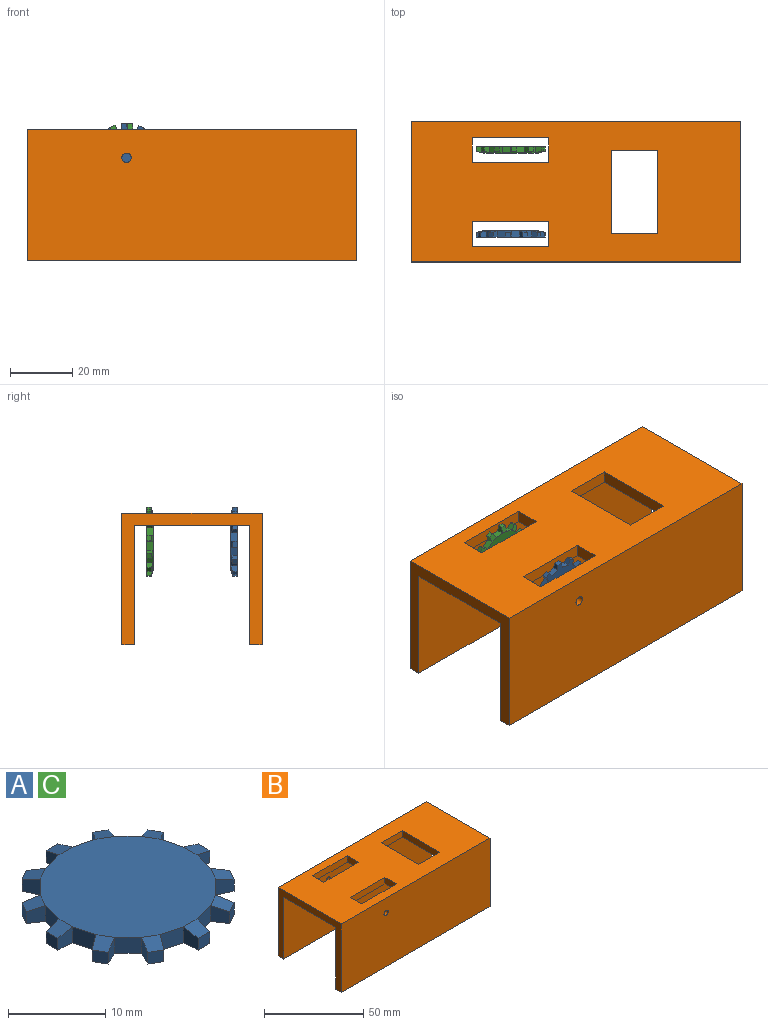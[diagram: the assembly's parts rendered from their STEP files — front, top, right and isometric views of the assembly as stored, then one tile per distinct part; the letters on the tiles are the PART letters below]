
ASSEMBLY  parts=3 mates=2
PART A: 62 faces, bbox 22.1x22.1x2 mm
  f0: plane 2.67x2mm, normal (0.26,0.97,0), area 5.5mm2, adj f1,f2,f5,f8
  f1: plane 18.09x18.09mm, normal (0,0,1), area 256.9mm2, adj f0,f4,f7,f9,f12,f14,f17,f19
  f2: plane 22.09x22.09mm, normal (0,0,-1), area 301.1mm2, adj f0,f3,f5,f6,f7,f8,f10,f11
  f3: plane 2x2mm, normal (-1,0.07,0), area 3.5mm2, adj f2,f4,f6,f57
  f4: plane 2x1.98mm, normal (0,0.26,0.97), area 3.8mm2, adj f1,f3,f5,f6
  f5: plane 2x2mm, normal (1,0.07,0), area 3.5mm2, adj f0,f2,f4,f6
  f6: plane 1.7x1.46mm, normal (0,1,0), area 2.5mm2, adj f2,f3,f4,f5
  f7: plane 2x1.96mm, normal (0.71,0.71,0), area 5.5mm2, adj f1,f2,f10,f13
  f8: plane 2x1.66mm, normal (-0.83,0.56,0), area 3.5mm2, adj f0,f2,f9,f11
  f9: plane 2.65x2.59mm, normal (0.13,0.22,0.97), area 3.8mm2, adj f1,f8,f10,f11
  f10: plane 2x1.8mm, normal (0.9,-0.44,0), area 3.5mm2, adj f2,f7,f9,f11
  f11: plane 1.47x1.46mm, normal (0.5,0.87,0), area 2.5mm2, adj f2,f8,f9,f10
  f12: plane 2.67x2mm, normal (0.97,0.26,0), area 5.5mm2, adj f1,f2,f15,f18
  f13: plane 2x1.8mm, normal (-0.44,0.9,0), area 3.5mm2, adj f2,f7,f14,f16
  f14: plane 2.65x2.59mm, normal (0.22,0.13,0.97), area 3.8mm2, adj f1,f13,f15,f16
  f15: plane 2x1.66mm, normal (0.56,-0.83,0), area 3.5mm2, adj f2,f12,f14,f16
  f16: plane 1.47x1.46mm, normal (0.87,0.5,0), area 2.5mm2, adj f2,f13,f14,f15
  f17: plane 2.67x2mm, normal (0.97,-0.26,0), area 5.5mm2, adj f1,f2,f20,f23
  f18: plane 2x2mm, normal (0.07,1,0), area 3.5mm2, adj f2,f12,f19,f21
  f19: plane 2x1.98mm, normal (0.26,0,0.97), area 3.8mm2, adj f1,f18,f20,f21
  f20: plane 2x2mm, normal (0.07,-1,0), area 3.5mm2, adj f2,f17,f19,f21
  f21: plane 1.7x1.46mm, normal (1,0,0), area 2.5mm2, adj f2,f18,f19,f20
  f22: plane 2x1.96mm, normal (0.71,-0.71,0), area 5.5mm2, adj f1,f2,f25,f28
  f23: plane 2x1.66mm, normal (0.56,0.83,0), area 3.5mm2, adj f2,f17,f24,f26
  f24: plane 2.65x2.59mm, normal (0.22,-0.13,0.97), area 3.8mm2, adj f1,f23,f25,f26
  f25: plane 2x1.8mm, normal (-0.44,-0.9,0), area 3.5mm2, adj f2,f22,f24,f26
  f26: plane 1.47x1.46mm, normal (0.87,-0.5,0), area 2.5mm2, adj f2,f23,f24,f25
  f27: plane 2.67x2mm, normal (0.26,-0.97,0), area 5.5mm2, adj f1,f2,f30,f33
  f28: plane 2x1.8mm, normal (0.9,0.44,0), area 3.5mm2, adj f2,f22,f29,f31
  f29: plane 2.65x2.59mm, normal (0.13,-0.22,0.97), area 3.8mm2, adj f1,f28,f30,f31
  f30: plane 2x1.66mm, normal (-0.83,-0.56,0), area 3.5mm2, adj f2,f27,f29,f31
  f31: plane 1.47x1.46mm, normal (0.5,-0.87,0), area 2.5mm2, adj f2,f28,f29,f30
  f32: plane 2.67x2mm, normal (-0.26,-0.97,0), area 5.5mm2, adj f1,f2,f35,f38
  f33: plane 2x2mm, normal (1,-0.07,0), area 3.5mm2, adj f2,f27,f34,f36
  f34: plane 2x1.98mm, normal (0,-0.26,0.97), area 3.8mm2, adj f1,f33,f35,f36
  f35: plane 2x2mm, normal (-1,-0.07,0), area 3.5mm2, adj f2,f32,f34,f36
  f36: plane 1.7x1.46mm, normal (0,-1,0), area 2.5mm2, adj f2,f33,f34,f35
  f37: plane 2x1.96mm, normal (-0.71,-0.71,0), area 5.5mm2, adj f1,f2,f40,f43
  f38: plane 2x1.66mm, normal (0.83,-0.56,0), area 3.5mm2, adj f2,f32,f39,f41
  f39: plane 2.65x2.59mm, normal (-0.13,-0.22,0.97), area 3.8mm2, adj f1,f38,f40,f41
  f40: plane 2x1.8mm, normal (-0.9,0.44,0), area 3.5mm2, adj f2,f37,f39,f41
  f41: plane 1.47x1.46mm, normal (-0.5,-0.87,0), area 2.5mm2, adj f2,f38,f39,f40
  f42: plane 2.67x2mm, normal (-0.97,-0.26,0), area 5.5mm2, adj f1,f2,f45,f48
  f43: plane 2x1.8mm, normal (0.44,-0.9,0), area 3.5mm2, adj f2,f37,f44,f46
  f44: plane 2.65x2.59mm, normal (-0.22,-0.13,0.97), area 3.8mm2, adj f1,f43,f45,f46
  f45: plane 2x1.66mm, normal (-0.56,0.83,0), area 3.5mm2, adj f2,f42,f44,f46
  f46: plane 1.47x1.46mm, normal (-0.87,-0.5,0), area 2.5mm2, adj f2,f43,f44,f45
  f47: plane 2.67x2mm, normal (-0.97,0.26,0), area 5.5mm2, adj f1,f2,f50,f53
  f48: plane 2x2mm, normal (-0.07,-1,0), area 3.5mm2, adj f2,f42,f49,f51
  f49: plane 2x1.98mm, normal (-0.26,0,0.97), area 3.8mm2, adj f1,f48,f50,f51
  f50: plane 2x2mm, normal (-0.07,1,0), area 3.5mm2, adj f2,f47,f49,f51
  f51: plane 1.7x1.46mm, normal (-1,0,0), area 2.5mm2, adj f2,f48,f49,f50
  f52: plane 2x1.96mm, normal (-0.71,0.71,0), area 5.5mm2, adj f1,f2,f55,f58
  f53: plane 2x1.66mm, normal (-0.56,-0.83,0), area 3.5mm2, adj f2,f47,f54,f56
  f54: plane 2.65x2.59mm, normal (-0.22,0.13,0.97), area 3.8mm2, adj f1,f53,f55,f56
  f55: plane 2x1.8mm, normal (0.44,0.9,0), area 3.5mm2, adj f2,f52,f54,f56
  f56: plane 1.47x1.46mm, normal (-0.87,0.5,0), area 2.5mm2, adj f2,f53,f54,f55
  f57: plane 2.67x2mm, normal (-0.26,0.97,0), area 5.5mm2, adj f1,f2,f3,f60
  f58: plane 2x1.8mm, normal (-0.9,-0.44,0), area 3.5mm2, adj f2,f52,f59,f61
  f59: plane 2.65x2.59mm, normal (-0.13,0.22,0.97), area 3.8mm2, adj f1,f58,f60,f61
  f60: plane 2x1.66mm, normal (0.83,0.56,0), area 3.5mm2, adj f2,f57,f59,f61
  f61: plane 1.47x1.46mm, normal (-0.5,0.87,0), area 2.5mm2, adj f2,f58,f59,f60
PART B: 24 faces, bbox 105.7x45x42.2 mm
  f0: plane 105.74x37mm, normal (0,0,-1), area 3116.2mm2, adj f1,f2,f3,f4,f5,f6,f7,f9
  f1: plane 8x4mm, normal (1,0,0), area 32mm2, adj f0,f2,f10,f11
  f2: plane 24.63x4mm, normal (0,-1,0), area 98.5mm2, adj f0,f1,f3,f11
  f3: plane 8x4mm, normal (-1,0,0), area 32mm2, adj f0,f2,f10,f11
  f4: plane 26.79x4mm, normal (-1,0,0), area 107.2mm2, adj f0,f5,f11,f18
  f5: plane 15x4mm, normal (0,1,0), area 60mm2, adj f0,f4,f6,f11
  f6: plane 26.79x4mm, normal (1,0,0), area 107.2mm2, adj f0,f5,f11,f18
  f7: plane 45x42.16mm, normal (-1,0,0), area 485.3mm2, adj f0,f8,f11,f13,f14,f19,f22,f23
  f8: plane 105.74x42.16mm, normal (0,-1,0), area 4450.7mm2, adj f7,f9,f11,f12,f13
  f9: plane 45x42.16mm, normal (1,0,0), area 485.3mm2, adj f0,f8,f11,f13,f14,f19,f22,f23
  f10: plane 24.63x4mm, normal (0,1,0), area 98.5mm2, adj f0,f1,f3,f11
  f11: plane 105.74x45mm, normal (0,0,1), area 3962.1mm2, adj f1,f2,f3,f4,f5,f6,f7,f8
  f12: cylinder r=1.5mm len=4mm, axis (0,-1,0), area 37.7mm2, adj f8,f14
  f13: plane 105.74x4mm, normal (0,0,-1), area 422.9mm2, adj f7,f8,f9,f14
  f14: plane 105.74x38.16mm, normal (0,1,0), area 4027.8mm2, adj f0,f7,f9,f12,f13
  f15: plane 8x4mm, normal (1,0,0), area 32mm2, adj f0,f11,f16,f20
  f16: plane 24.63x4mm, normal (0,1,0), area 98.5mm2, adj f0,f11,f15,f17
  f17: plane 8x4mm, normal (-1,0,0), area 32mm2, adj f0,f11,f16,f20
  f18: plane 15x4mm, normal (0,-1,0), area 60mm2, adj f0,f4,f6,f11
  f19: plane 105.74x42.16mm, normal (0,1,0), area 4450.7mm2, adj f7,f9,f11,f21,f22
  f20: plane 24.63x4mm, normal (0,-1,0), area 98.5mm2, adj f0,f11,f15,f17
  f21: cylinder r=1.5mm len=4mm, axis (0,1,0), area 37.7mm2, adj f19,f23
  f22: plane 105.74x4mm, normal (0,0,-1), area 422.9mm2, adj f7,f9,f19,f23
  f23: plane 105.74x38.16mm, normal (0,-1,0), area 4027.8mm2, adj f0,f7,f9,f21,f22
PART C: same geometry as A
PLACE A rot(axis=(-0.22,0.69,0.69),155.7deg) t=(-96.59,8,67.61)mm
PLACE B t=(-74.86,37.34,38.16)mm
PLACE C rot(axis=(0.73,0.48,-0.48),107.4deg) t=(-36.41,37,50.58)mm
MATE revolute A.f1 <-> B.f12  axis (0,1,0) through (-73.87,10,33.06)mm
MATE revolute C.f1 <-> B.f12  axis (0,-1,0) through (-73.87,35,33.06)mm
